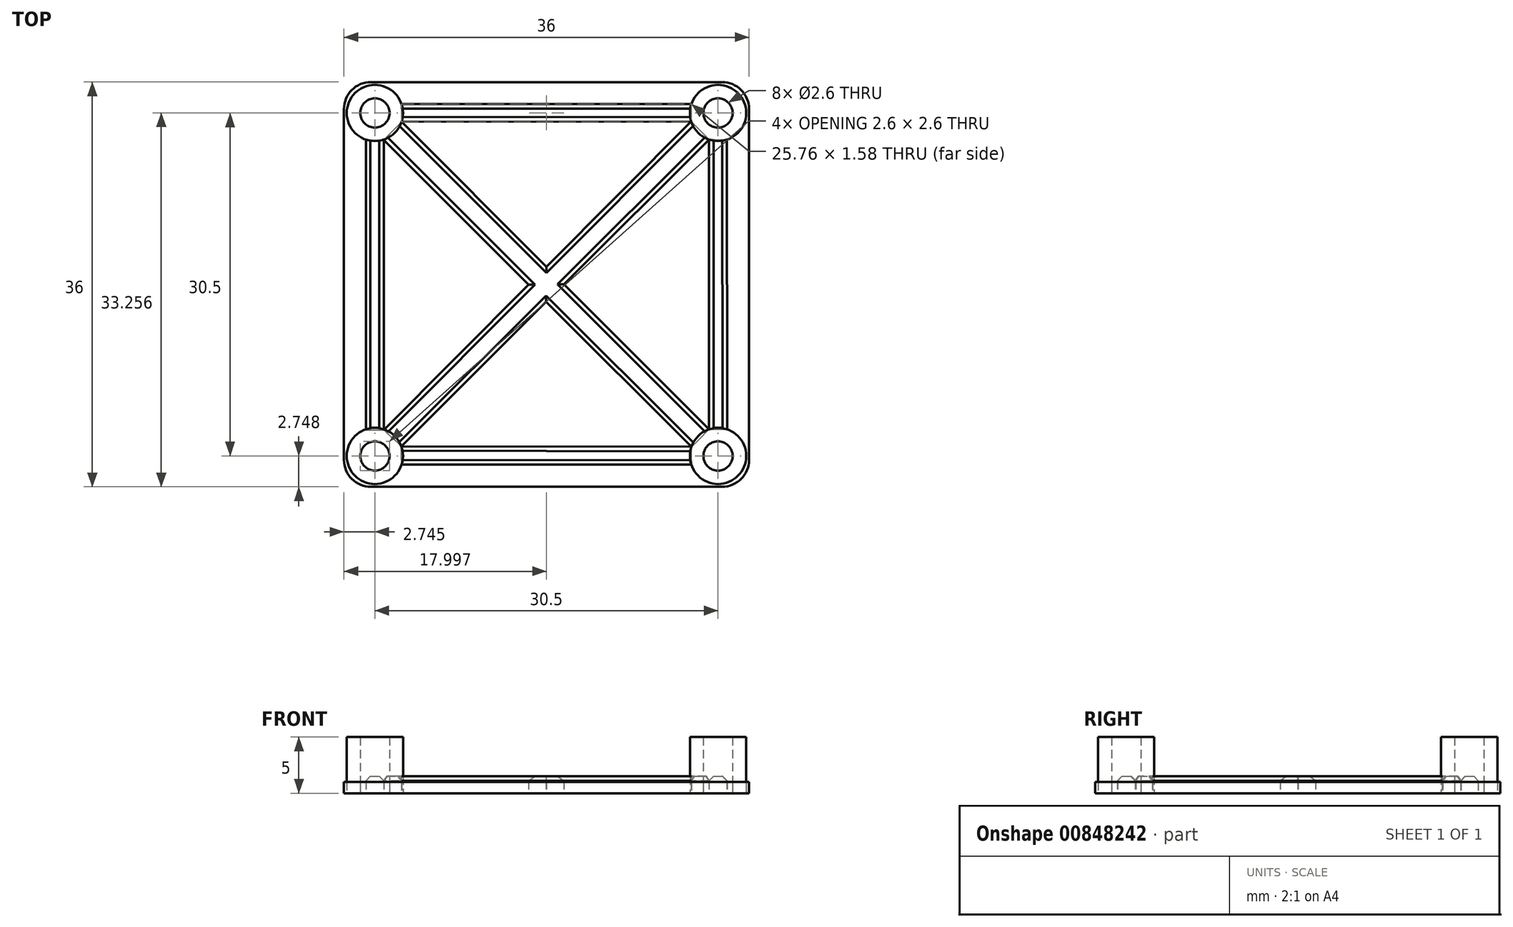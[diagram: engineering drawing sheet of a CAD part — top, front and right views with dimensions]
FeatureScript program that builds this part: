
annotation { "Feature Type Name" : "Feature", "Feature Type Description" : "" }
export const myFeature = defineFeature(function(context is Context, id is Id, definition is map)
    precondition{}
    {
        {
            var Q0;
            Q0=qCreatedBy(makeId("Top.planeOp"),FACE);
            var sketch = newSketch(context, id + "F0", { "sketchPlane" : qUnion([Q0])});
            skPoint(sketch, "E0", {"position": v(-15.68, 14.67) * mm});
            skPoint(sketch, "E1", {"position": v(14.82, 14.67) * mm});
            skPoint(sketch, "E2", {"position": v(14.82, -15.83) * mm});
            skPoint(sketch, "E3", {"position": v(-15.68, -15.83) * mm});
            skCircle(sketch, "E4", {"center": v(-15.68, 14.67) * mm, "radius": 2.5 * mm});
            skCircle(sketch, "E5", {"center": v(14.82, 14.67) * mm, "radius": 2.5 * mm});
            skCircle(sketch, "E6", {"center": v(14.82, -15.83) * mm, "radius": 2.5 * mm});
            skCircle(sketch, "E7", {"center": v(-15.68, -15.83) * mm, "radius": 2.5 * mm});
            skSolve(sketch);
        }
        {
            var Q0;
            Q0=qCreatedBy(makeId("Top.planeOp"),FACE);
            var sketch = newSketch(context, id + "F1", { "sketchPlane" : qUnion([Q0])});
            skLineSegment(sketch, "E8.0", {"start": v(-18.43, -18.58) * mm, "end": v(17.57, -18.58) * mm});
            skLineSegment(sketch, "E8.1", {"start": v(-18.43, 17.42) * mm, "end": v(-18.43, -18.58) * mm});
            skLineSegment(sketch, "E8.2", {"start": v(17.57, 17.42) * mm, "end": v(-18.43, 17.42) * mm});
            skLineSegment(sketch, "E8.3", {"start": v(17.57, -18.58) * mm, "end": v(17.57, 17.42) * mm});
            skLineSegment(sketch, "E9", {"start": v(-16.48, -13.5) * mm, "end": v(-16.48, 12.26) * mm});
            skLineSegment(sketch, "E10", {"start": v(-14.88, -13.5) * mm, "end": v(-14.88, 12.26) * mm});
            skLineSegment(sketch, "E11", {"start": v(-13.3, -16.6) * mm, "end": v(12.44, -16.6) * mm});
            skLineSegment(sketch, "E12", {"start": v(-13.34, -14.97) * mm, "end": v(12.45, -15.03) * mm});
            skLineSegment(sketch, "E13", {"start": v(14.02, -13.46) * mm, "end": v(14.02, 12.3) * mm});
            skLineSegment(sketch, "E14", {"start": v(15.62, -13.46) * mm, "end": v(15.58, 12.29) * mm});
            skLineSegment(sketch, "E15", {"start": v(-13.31, 15.47) * mm, "end": v(12.45, 15.47) * mm});
            skLineSegment(sketch, "E16", {"start": v(-13.31, 13.89) * mm, "end": v(12.43, 13.92) * mm});
            skLineSegment(sketch, "E17", {"start": v(-16.48, -13.5) * mm, "end": v(-14.88, -13.5) * mm});
            skLineSegment(sketch, "E18", {"start": v(-13.3, -16.6) * mm, "end": v(-13.34, -14.97) * mm});
            skLineSegment(sketch, "E19", {"start": v(-16.48, 12.26) * mm, "end": v(-14.88, 12.26) * mm});
            skLineSegment(sketch, "E20", {"start": v(12.44, -16.6) * mm, "end": v(12.45, -15.03) * mm});
            skLineSegment(sketch, "E21", {"start": v(14.02, -13.46) * mm, "end": v(15.62, -13.46) * mm});
            skLineSegment(sketch, "E22", {"start": v(14.02, 12.3) * mm, "end": v(15.58, 12.29) * mm});
            skLineSegment(sketch, "E23", {"start": v(12.43, 13.92) * mm, "end": v(12.45, 15.47) * mm});
            skLineSegment(sketch, "E24", {"start": v(-14.88, -13.5) * mm, "end": v(12.43, 13.92) * mm});
            skLineSegment(sketch, "E25", {"start": v(-13.34, -14.97) * mm, "end": v(14.02, 12.3) * mm});
            skLineSegment(sketch, "E26", {"start": v(12.45, -15.03) * mm, "end": v(-14.88, 12.26) * mm});
            skLineSegment(sketch, "E27", {"start": v(-13.31, 13.89) * mm, "end": v(14.02, -13.46) * mm});
            skLineSegment(sketch, "E28", {"start": v(-13.34, -14.97) * mm, "end": v(-14.88, -13.5) * mm});
            skLineSegment(sketch, "E29", {"start": v(-14.88, 12.26) * mm, "end": v(-13.31, 13.89) * mm});
            skLineSegment(sketch, "E30", {"start": v(12.45, -15.03) * mm, "end": v(14.02, -13.46) * mm});
            skLineSegment(sketch, "E31", {"start": v(14.02, 12.3) * mm, "end": v(12.43, 13.92) * mm});
            skLineSegment(sketch, "E32", {"start": v(-13.31, 13.89) * mm, "end": v(-13.31, 15.47) * mm});
            skSolve(sketch);
        }
        {
            var Q0;
            Q0=qCreatedBy(makeId("Top.planeOp"),FACE);
            var sketch = newSketch(context, id + "F2", { "sketchPlane" : qUnion([Q0])});
            skCircle(sketch, "E33", {"center": v(-15.68, 14.67) * mm, "radius": 1.25 * mm});
            skCircle(sketch, "E34", {"center": v(14.82, 14.67) * mm, "radius": 1.25 * mm});
            skCircle(sketch, "E35", {"center": v(14.82, -15.83) * mm, "radius": 1.25 * mm});
            skCircle(sketch, "E36", {"center": v(-15.68, -15.83) * mm, "radius": 1.25 * mm});
            skSolve(sketch);
        }
        {
            var Q0;
            {var subQ0=sQuery(id+"F1.wireOp",EDGE,"E16");Q0=makeQuery(id+"F1.imprint","IMPRINT",FACE,{"disambiguationData":[TD([[makeQuery(id+"F1.imprint","IMPRINT",EDGE,{"derivedFrom":subQ0}),-1.0]])]});}
            var Q1;
            {var subQ0=sQuery(id+"F1.wireOp",EDGE,"E10");Q1=makeQuery(id+"F1.imprint","IMPRINT",FACE,{"disambiguationData":[TD([[makeQuery(id+"F1.imprint","IMPRINT",EDGE,{"derivedFrom":subQ0}),-1.0]])]});}
            var Q2;
            Q2=makeQuery(id+"F1.imprint","IMPRINT",FACE,{"disambiguationData":[TD([[makeQuery(id+"F1.imprint","IMPRINT",EDGE,{"derivedFrom":sQuery(id+"F1.wireOp",EDGE,"E9")}),-1.0]])]});
            var Q3;
            {var subQ0=sQuery(id+"F1.wireOp",EDGE,"E28");Q3=makeQuery(id+"F1.imprint","IMPRINT",FACE,{"disambiguationData":[TD([[makeQuery(id+"F1.imprint","IMPRINT",EDGE,{"derivedFrom":subQ0}),-1.0]])]});}
            var Q4;
            Q4=makeQuery(id+"F1.imprint","IMPRINT",FACE,{"disambiguationData":[TD([[makeQuery(id+"F1.imprint","IMPRINT",EDGE,{"derivedFrom":sQuery(id+"F1.wireOp",EDGE,"E11")}),1.0]])]});
            var Q5;
            {var subQ0=sQuery(id+"F1.wireOp",EDGE,"E12");Q5=makeQuery(id+"F1.imprint","IMPRINT",FACE,{"disambiguationData":[TD([[makeQuery(id+"F1.imprint","IMPRINT",EDGE,{"derivedFrom":subQ0}),1.0]])]});}
            var Q6;
            {var subQ5=sQuery(id+"F1.wireOp",EDGE,"E30");Q6=makeQuery(id+"F1.imprint","IMPRINT",FACE,{"disambiguationData":[TD([[makeQuery(id+"F1.imprint","IMPRINT",EDGE,{"derivedFrom":subQ5}),1.0]])]});}
            var Q7;
            {var subQ0=sQuery(id+"F1.wireOp",EDGE,"E13");Q7=makeQuery(id+"F1.imprint","IMPRINT",FACE,{"disambiguationData":[TD([[makeQuery(id+"F1.imprint","IMPRINT",EDGE,{"derivedFrom":subQ0}),1.0]])]});}
            var Q8;
            Q8=makeQuery(id+"F1.imprint","IMPRINT",FACE,{"disambiguationData":[TD([[makeQuery(id+"F1.imprint","IMPRINT",EDGE,{"derivedFrom":sQuery(id+"F1.wireOp",EDGE,"E13")}),-1.0]])]});
            var Q9;
            {var subQ0=sQuery(id+"F1.wireOp",EDGE,"E31");Q9=makeQuery(id+"F1.imprint","IMPRINT",FACE,{"disambiguationData":[TD([[makeQuery(id+"F1.imprint","IMPRINT",EDGE,{"derivedFrom":subQ0}),1.0]])]});}
            var Q10;
            {var subQ5=sQuery(id+"F1.wireOp",EDGE,"E29");Q10=makeQuery(id+"F1.imprint","IMPRINT",FACE,{"disambiguationData":[TD([[makeQuery(id+"F1.imprint","IMPRINT",EDGE,{"derivedFrom":subQ5}),-1.0]])]});}
            var Q11;
            {var subQ0=sQuery(id+"F1.wireOp",EDGE,"E26");var subQ1=sQuery(id+"F1.wireOp",EDGE,"E24");var subQ2=makeQuery(id+"F1.imprint","INTERSECT",VERTEX,{"derivedFrom":[subQ1,subQ0]});Q11=makeQuery(id+"F1.imprint","IMPRINT",FACE,{"disambiguationData":[TD([[makeQuery(id+"F1.imprint","IMPRINT",EDGE,{"disambiguationData":[TD([[subQ2,-1.0]])],"derivedFrom":subQ1}),-1.0]])]});}
            var Q12;
            Q12=makeQuery(id+"F1.imprint","IMPRINT",FACE,{"disambiguationData":[TD([[makeQuery(id+"F1.imprint","IMPRINT",EDGE,{"derivedFrom":sQuery(id+"F1.wireOp",EDGE,"E8.0")}),1.0]])]});
            extrude(context, id + "F3", {"entities" : qUnion([Q0, Q1, Q2, Q3, Q4, Q5, Q6, Q7, Q8, Q9, Q10, Q11, Q12]), "depth" : 1 * mm, "offsetDistance" : 25 * mm});
        }
        {
            var Q0;
            Q0=makeQuery(id+"F1.imprint","IMPRINT",FACE,{"disambiguationData":[TD([[makeQuery(id+"F1.imprint","IMPRINT",EDGE,{"derivedFrom":sQuery(id+"F1.wireOp",EDGE,"E9")}),-1.0]])]});
            var Q1;
            Q1=makeQuery(id+"F1.imprint","IMPRINT",FACE,{"disambiguationData":[TD([[makeQuery(id+"F1.imprint","IMPRINT",EDGE,{"derivedFrom":sQuery(id+"F1.wireOp",EDGE,"E11")}),1.0]])]});
            var Q2;
            {var subQ0=sQuery(id+"F1.wireOp",EDGE,"E28");Q2=makeQuery(id+"F1.imprint","IMPRINT",FACE,{"disambiguationData":[TD([[makeQuery(id+"F1.imprint","IMPRINT",EDGE,{"derivedFrom":subQ0}),-1.0]])]});}
            var Q3;
            {var subQ5=sQuery(id+"F1.wireOp",EDGE,"E30");Q3=makeQuery(id+"F1.imprint","IMPRINT",FACE,{"disambiguationData":[TD([[makeQuery(id+"F1.imprint","IMPRINT",EDGE,{"derivedFrom":subQ5}),1.0]])]});}
            var Q4;
            {var subQ0=sQuery(id+"F1.wireOp",EDGE,"E26");var subQ1=sQuery(id+"F1.wireOp",EDGE,"E24");var subQ2=makeQuery(id+"F1.imprint","INTERSECT",VERTEX,{"derivedFrom":[subQ1,subQ0]});Q4=makeQuery(id+"F1.imprint","IMPRINT",FACE,{"disambiguationData":[TD([[makeQuery(id+"F1.imprint","IMPRINT",EDGE,{"disambiguationData":[TD([[subQ2,-1.0]])],"derivedFrom":subQ1}),-1.0]])]});}
            var Q5;
            {var subQ5=sQuery(id+"F1.wireOp",EDGE,"E29");Q5=makeQuery(id+"F1.imprint","IMPRINT",FACE,{"disambiguationData":[TD([[makeQuery(id+"F1.imprint","IMPRINT",EDGE,{"derivedFrom":subQ5}),-1.0]])]});}
            var Q6;
            {var subQ0=sQuery(id+"F1.wireOp",EDGE,"E31");Q6=makeQuery(id+"F1.imprint","IMPRINT",FACE,{"disambiguationData":[TD([[makeQuery(id+"F1.imprint","IMPRINT",EDGE,{"derivedFrom":subQ0}),1.0]])]});}
            var Q7;
            Q7=makeQuery(id+"F1.imprint","IMPRINT",FACE,{"disambiguationData":[TD([[makeQuery(id+"F1.imprint","IMPRINT",EDGE,{"derivedFrom":sQuery(id+"F1.wireOp",EDGE,"E15")}),-1.0]])]});
            var Q8;
            Q8=makeQuery(id+"F1.imprint","IMPRINT",FACE,{"disambiguationData":[TD([[makeQuery(id+"F1.imprint","IMPRINT",EDGE,{"derivedFrom":sQuery(id+"F1.wireOp",EDGE,"E13")}),-1.0]])]});
            extrude(context, id + "F4", {"entities" : qUnion([Q0, Q1, Q2, Q3, Q4, Q5, Q6, Q7, Q8]), "depth" : 1.5 * mm, "offsetDistance" : 25 * mm});
        }
        {
            var Q0;
            Q0 = qSketchRegion(id + "F0", true);
            extrude(context, id + "F5", {"entities" : qUnion([Q0]), "depth" : 5 * mm, "offsetDistance" : 25 * mm});
        }
        {
            var Q0;
            Q0=sQuery(id+"F2.wireOp",VERTEX,"E34.center");
            var Q1;
            Q1=sQuery(id+"F2.wireOp",VERTEX,"E33.center");
            var Q2;
            Q2=sQuery(id+"F2.wireOp",VERTEX,"E36.center");
            var Q3;
            Q3=sQuery(id+"F2.wireOp",VERTEX,"E35.center");
            var Q4;
            Q4=makeQuery(id+"F3.opExtrude","SWEPT_BODY",BODY,{"disambiguationData":[OSD([sQuery(id+"F1.wireOp",EDGE,"E8.0"),sQuery(id+"F1.wireOp",EDGE,"E8.1"),sQuery(id+"F1.wireOp",EDGE,"E8.2"),sQuery(id+"F1.wireOp",EDGE,"E8.3"),sQuery(id+"F1.wireOp",EDGE,"E15"),sQuery(id+"F1.wireOp",EDGE,"E16"),sQuery(id+"F1.wireOp",EDGE,"E23"),sQuery(id+"F1.wireOp",EDGE,"E32")])]});
            var Q5;
            Q5=makeQuery(id+"F5.opExtrude","SWEPT_BODY",BODY,{"disambiguationData":[OSD([sQuery(id+"F0.wireOp",EDGE,"E5")])]});
            var Q6;
            Q6=makeQuery(id+"F5.opExtrude","SWEPT_BODY",BODY,{"disambiguationData":[OSD([sQuery(id+"F0.wireOp",EDGE,"E4")])]});
            var Q7;
            Q7=makeQuery(id+"F5.opExtrude","SWEPT_BODY",BODY,{"disambiguationData":[OSD([sQuery(id+"F0.wireOp",EDGE,"E7")])]});
            var Q8;
            Q8=makeQuery(id+"F5.opExtrude","SWEPT_BODY",BODY,{"disambiguationData":[OSD([sQuery(id+"F0.wireOp",EDGE,"E6")])]});
            hole(context, id + "F6", {"style" : HoleStyle.SIMPLE, "endStyle" : HoleEndStyle.THROUGH, "oppositeDirection" : true, "holeDiameter" : 2.6 * mm, "majorDiameter" : 5 * mm, "isTappedThrough" : true, "tappedDepth" : 12 * mm, "tapClearance" : 3, "locations" : qUnion([Q0, Q1, Q2, Q3]), "scope" : qUnion([Q4, Q5, Q6, Q7, Q8])});
        }
        {
            var Q0;
            Q0=makeQuery(id+"F3.opExtrude","SWEPT_EDGE",EDGE,{"disambiguationData":[OSD([sQuery(id+"F1.wireOp",EDGE,"E8.0"),sQuery(id+"F1.wireOp",EDGE,"E8.3")])]});
            var Q1;
            Q1=makeQuery(id+"F3.opExtrude","SWEPT_EDGE",EDGE,{"disambiguationData":[OSD([sQuery(id+"F1.wireOp",EDGE,"E8.2"),sQuery(id+"F1.wireOp",EDGE,"E8.3")])]});
            var Q2;
            Q2=makeQuery(id+"F3.opExtrude","SWEPT_EDGE",EDGE,{"disambiguationData":[OSD([sQuery(id+"F1.wireOp",EDGE,"E8.0"),sQuery(id+"F1.wireOp",EDGE,"E8.1")])]});
            var Q3;
            Q3=makeQuery(id+"F3.opExtrude","SWEPT_EDGE",EDGE,{"disambiguationData":[OSD([sQuery(id+"F1.wireOp",EDGE,"E8.1"),sQuery(id+"F1.wireOp",EDGE,"E8.2")])]});
            fillet(context, id + "F7", {"entities" : qUnion([Q0, Q1, Q2, Q3]), "radius" : 2.4 * mm, "tangentPropagation" : true, "allowEdgeOverflow" : false});
        }
        {
            var Q0;
            Q0=makeQuery(id+"F4.opExtrude","CAP_EDGE",EDGE,{"disambiguationData":[OSD([sQuery(id+"F1.wireOp",EDGE,"E10")])],"isStart":false});
            var Q1;
            Q1=makeQuery(id+"F4.opExtrude","CAP_EDGE",EDGE,{"disambiguationData":[OSD([sQuery(id+"F1.wireOp",EDGE,"E9")])],"isStart":false});
            var Q2;
            {var subQ0=sQuery(id+"F1.wireOp",EDGE,"E24");Q2=makeQuery(id+"F4.opExtrude","CAP_EDGE",EDGE,{"disambiguationData":[OSD([subQ0]),TDD([makeQuery(id+"F1.imprint","IMPRINT",EDGE,{"disambiguationData":[TD([[makeQuery(id+"F1.imprint","INTERSECT",VERTEX,{"derivedFrom":[subQ0,sQuery(id+"F1.wireOp",EDGE,"E26")]}),1.0]])],"derivedFrom":subQ0})])],"isStart":false});}
            var Q3;
            {var subQ0=sQuery(id+"F1.wireOp",EDGE,"E25");Q3=makeQuery(id+"F4.opExtrude","CAP_EDGE",EDGE,{"disambiguationData":[OSD([subQ0]),TDD([makeQuery(id+"F1.imprint","IMPRINT",EDGE,{"disambiguationData":[TD([[makeQuery(id+"F1.imprint","INTERSECT",VERTEX,{"derivedFrom":[subQ0,sQuery(id+"F1.wireOp",EDGE,"E26")]}),1.0]])],"derivedFrom":subQ0})])],"isStart":false});}
            var Q4;
            {var subQ0=sQuery(id+"F1.wireOp",EDGE,"E26");Q4=makeQuery(id+"F4.opExtrude","CAP_EDGE",EDGE,{"disambiguationData":[OSD([subQ0]),TDD([makeQuery(id+"F1.imprint","IMPRINT",EDGE,{"disambiguationData":[TD([[makeQuery(id+"F1.imprint","INTERSECT",VERTEX,{"derivedFrom":[sQuery(id+"F1.wireOp",EDGE,"E24"),subQ0]}),-1.0]])],"derivedFrom":subQ0})])],"isStart":false});}
            var Q5;
            {var subQ0=sQuery(id+"F1.wireOp",EDGE,"E27");Q5=makeQuery(id+"F4.opExtrude","CAP_EDGE",EDGE,{"disambiguationData":[OSD([subQ0]),TDD([makeQuery(id+"F1.imprint","IMPRINT",EDGE,{"disambiguationData":[TD([[makeQuery(id+"F1.imprint","INTERSECT",VERTEX,{"derivedFrom":[sQuery(id+"F1.wireOp",EDGE,"E24"),subQ0]}),1.0]])],"derivedFrom":subQ0})])],"isStart":false});}
            var Q6;
            {var subQ0=sQuery(id+"F1.wireOp",EDGE,"E24");Q6=makeQuery(id+"F4.opExtrude","CAP_EDGE",EDGE,{"disambiguationData":[OSD([subQ0]),TDD([makeQuery(id+"F1.imprint","IMPRINT",EDGE,{"disambiguationData":[TD([[makeQuery(id+"F1.imprint","INTERSECT",VERTEX,{"derivedFrom":[subQ0,sQuery(id+"F1.wireOp",EDGE,"E27")]}),-1.0]])],"derivedFrom":subQ0})])],"isStart":false});}
            var Q7;
            {var subQ0=sQuery(id+"F1.wireOp",EDGE,"E25");Q7=makeQuery(id+"F4.opExtrude","CAP_EDGE",EDGE,{"disambiguationData":[OSD([subQ0]),TDD([makeQuery(id+"F1.imprint","IMPRINT",EDGE,{"disambiguationData":[TD([[makeQuery(id+"F1.imprint","INTERSECT",VERTEX,{"derivedFrom":[subQ0,sQuery(id+"F1.wireOp",EDGE,"E27")]}),-1.0]])],"derivedFrom":subQ0})])],"isStart":false});}
            var Q8;
            {var subQ0=sQuery(id+"F1.wireOp",EDGE,"E27");Q8=makeQuery(id+"F4.opExtrude","CAP_EDGE",EDGE,{"disambiguationData":[OSD([subQ0]),TDD([makeQuery(id+"F1.imprint","IMPRINT",EDGE,{"disambiguationData":[TD([[makeQuery(id+"F1.imprint","INTERSECT",VERTEX,{"derivedFrom":[sQuery(id+"F1.wireOp",EDGE,"E25"),subQ0]}),-1.0]])],"derivedFrom":subQ0})])],"isStart":false});}
            var Q9;
            {var subQ0=sQuery(id+"F1.wireOp",EDGE,"E26");Q9=makeQuery(id+"F4.opExtrude","CAP_EDGE",EDGE,{"disambiguationData":[OSD([subQ0]),TDD([makeQuery(id+"F1.imprint","IMPRINT",EDGE,{"disambiguationData":[TD([[makeQuery(id+"F1.imprint","INTERSECT",VERTEX,{"derivedFrom":[sQuery(id+"F1.wireOp",EDGE,"E25"),subQ0]}),1.0]])],"derivedFrom":subQ0})])],"isStart":false});}
            var Q10;
            Q10=makeQuery(id+"F4.opExtrude","CAP_EDGE",EDGE,{"disambiguationData":[OSD([sQuery(id+"F1.wireOp",EDGE,"E12")])],"isStart":false});
            var Q11;
            Q11=makeQuery(id+"F4.opExtrude","CAP_EDGE",EDGE,{"disambiguationData":[OSD([sQuery(id+"F1.wireOp",EDGE,"E11")])],"isStart":false});
            var Q12;
            Q12=makeQuery(id+"F4.opExtrude","CAP_EDGE",EDGE,{"disambiguationData":[OSD([sQuery(id+"F1.wireOp",EDGE,"E13")])],"isStart":false});
            var Q13;
            Q13=makeQuery(id+"F4.opExtrude","CAP_EDGE",EDGE,{"disambiguationData":[OSD([sQuery(id+"F1.wireOp",EDGE,"E14")])],"isStart":false});
            var Q14;
            Q14=makeQuery(id+"F4.opExtrude","CAP_EDGE",EDGE,{"disambiguationData":[OSD([sQuery(id+"F1.wireOp",EDGE,"E15")])],"isStart":false});
            var Q15;
            Q15=makeQuery(id+"F4.opExtrude","CAP_EDGE",EDGE,{"disambiguationData":[OSD([sQuery(id+"F1.wireOp",EDGE,"E16")])],"isStart":false});
            chamfer(context, id + "F8", {"entities" : qUnion([Q0, Q1, Q2, Q3, Q4, Q5, Q6, Q7, Q8, Q9, Q10, Q11, Q12, Q13, Q14, Q15]), "width" : 0.4 * mm, "tangentPropagation" : true});
        }
    });
